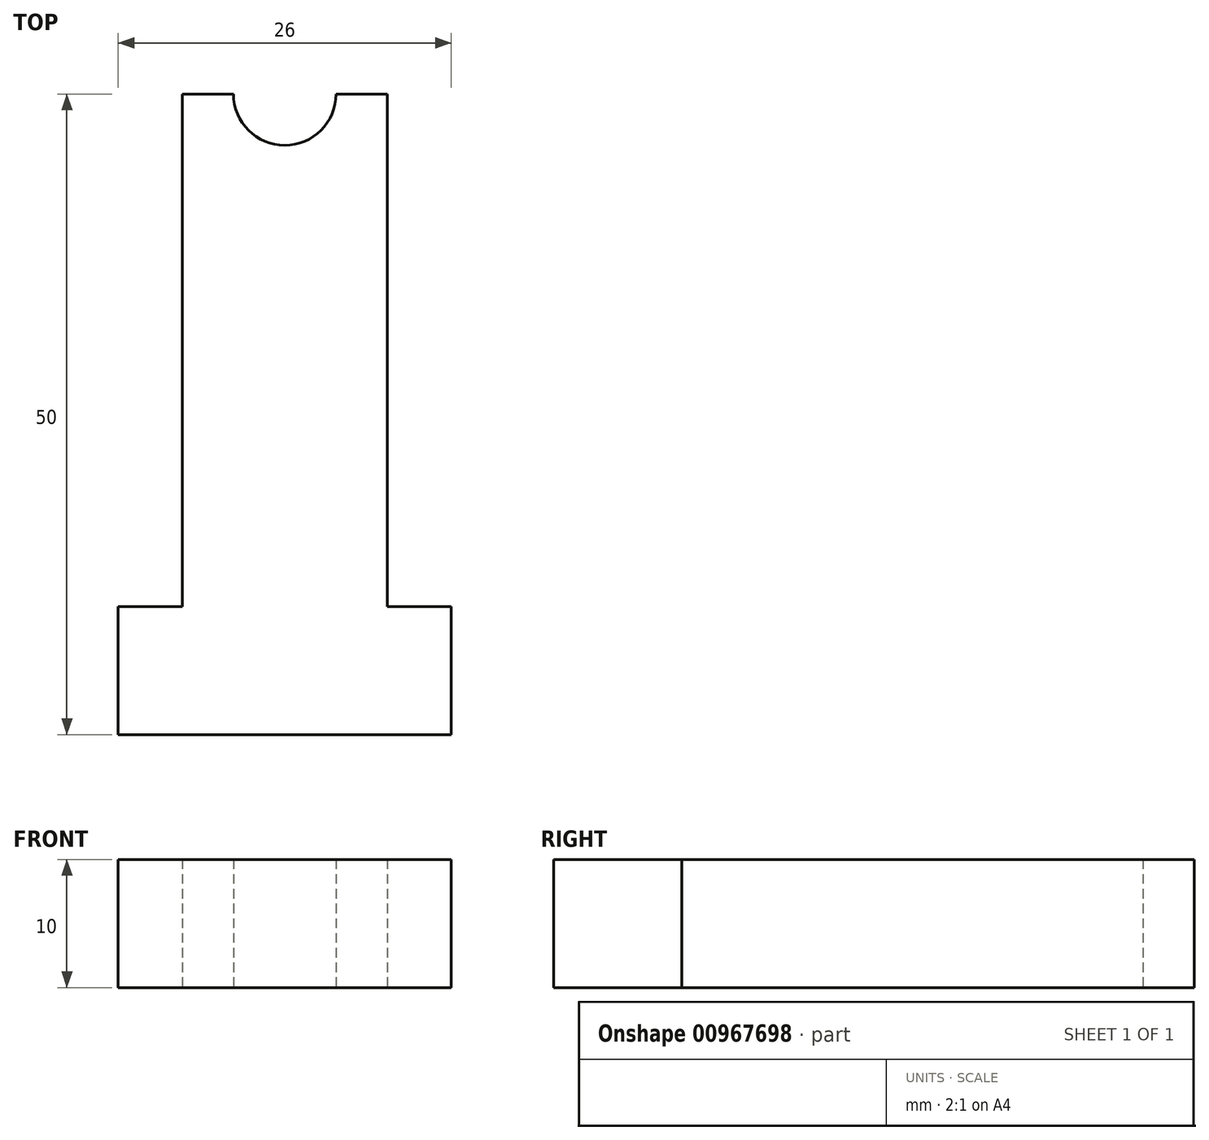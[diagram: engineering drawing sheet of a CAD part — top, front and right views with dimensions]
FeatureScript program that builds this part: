
annotation { "Feature Type Name" : "Feature", "Feature Type Description" : "" }
export const myFeature = defineFeature(function(context is Context, id is Id, definition is map)
    precondition{}
    {
        {
            var Q0;
            Q0=qCreatedBy(makeId("Top.planeOp"),FACE);
            var sketch = newSketch(context, id + "F0", { "sketchPlane" : qUnion([Q0])});
            skLineSegment(sketch, "E0.top", {"start": v(8, 20) * mm, "end": v(4, 20) * mm});
            skLineSegment(sketch, "E0.left", {"start": v(8, -20) * mm, "end": v(8, 20) * mm});
            skLineSegment(sketch, "E0.right", {"start": v(-8, -20) * mm, "end": v(-8, 20) * mm});
            skPoint(sketch, "E0.middle", {"position": v(0, 0) * mm});
            skArc(sketch, "E1", {"start": v(4, 20) * mm, "mid": v(0, 16) * mm, "end": v(-4, 20) * mm});
            skLineSegment(sketch, "E2.trimOffspring", {"start": v(-4, 20) * mm, "end": v(-8, 20) * mm});
            skLineSegment(sketch, "E3", {"start": v(0, 0) * mm, "end": v(-0.11, -46.11) * mm, "construction": true});
            skPoint(sketch, "E4.middle", {"position": v(-0.03, -14.15) * mm});
            skLineSegment(sketch, "E5", {"start": v(-8, -20) * mm, "end": v(-13, -20) * mm});
            skLineSegment(sketch, "E6", {"start": v(-13, -20) * mm, "end": v(-13, -30) * mm});
            skLineSegment(sketch, "E7", {"start": v(-13, -30) * mm, "end": v(13, -30) * mm});
            skLineSegment(sketch, "E8", {"start": v(13, -30) * mm, "end": v(13, -20) * mm});
            skLineSegment(sketch, "E9", {"start": v(13, -20) * mm, "end": v(8, -20) * mm});
            skSolve(sketch);
        }
        {
            var Q0;
            Q0=makeQuery(id+"F0.imprint","IMPRINT",FACE,{"disambiguationData":[TD([[makeQuery(id+"F0.imprint","IMPRINT",EDGE,{"derivedFrom":sQuery(id+"F0.wireOp",EDGE,"E0.top")}),1.0]])]});
            extrude(context, id + "F1", {"entities" : qUnion([Q0]), "depth" : 10 * mm, "offsetDistance" : 25 * mm});
        }
    });
